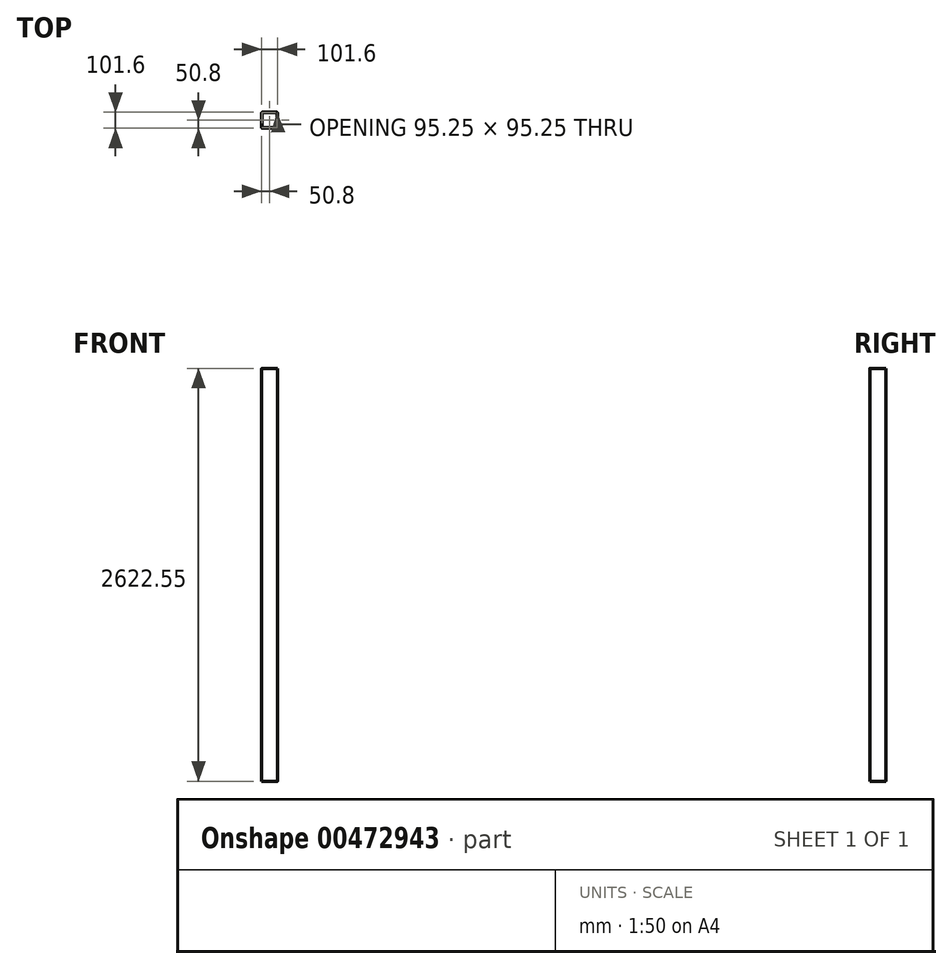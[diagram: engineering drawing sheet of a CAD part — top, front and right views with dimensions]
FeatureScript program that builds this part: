
annotation { "Feature Type Name" : "Feature", "Feature Type Description" : "" }
export const myFeature = defineFeature(function(context is Context, id is Id, definition is map)
    precondition{}
    {
        {
            var Q0;
            Q0=qCreatedBy(makeId("Top.planeOp"),FACE);
            var sketch = newSketch(context, id + "F0", { "sketchPlane" : qUnion([Q0])});
            skLineSegment(sketch, "E0.bottom", {"start": v(-50.8, -50.8) * mm, "end": v(50.8, -50.8) * mm});
            skLineSegment(sketch, "E0.top", {"start": v(-50.8, 50.8) * mm, "end": v(50.8, 50.8) * mm});
            skLineSegment(sketch, "E0.left", {"start": v(-50.8, -50.8) * mm, "end": v(-50.8, 50.8) * mm});
            skLineSegment(sketch, "E0.right", {"start": v(50.8, -50.8) * mm, "end": v(50.8, 50.8) * mm});
            skPoint(sketch, "E0.middle", {"position": v(0, 0) * mm});
            skLineSegment(sketch, "E1.bottom", {"start": v(-47.63, -47.63) * mm, "end": v(47.63, -47.63) * mm});
            skLineSegment(sketch, "E1.top", {"start": v(-47.63, 47.63) * mm, "end": v(47.63, 47.63) * mm});
            skLineSegment(sketch, "E1.left", {"start": v(-47.63, -47.63) * mm, "end": v(-47.63, 47.63) * mm});
            skLineSegment(sketch, "E1.right", {"start": v(47.63, -47.63) * mm, "end": v(47.63, 47.63) * mm});
            skSolve(sketch);
        }
        {
            var Q0;
            Q0=makeQuery(id+"F0.imprint","IMPRINT",FACE,{"disambiguationData":[TD([[makeQuery(id+"F0.imprint","IMPRINT",EDGE,{"derivedFrom":sQuery(id+"F0.wireOp",EDGE,"E0.bottom")}),1.0]])]});
            extrude(context, id + "F1", {"entities" : qUnion([Q0]), "depth" : 2622.55 * mm});
        }
        {
            var Q0;
            Q0=makeQuery(id+"F1.opExtrude","SWEPT_EDGE",EDGE,{"disambiguationData":[OSD([sQuery(id+"F0.wireOp",EDGE,"E0.bottom"),sQuery(id+"F0.wireOp",EDGE,"E0.left")])]});
            var Q1;
            Q1=makeQuery(id+"F1.opExtrude","SWEPT_EDGE",EDGE,{"disambiguationData":[OSD([sQuery(id+"F0.wireOp",EDGE,"E0.bottom"),sQuery(id+"F0.wireOp",EDGE,"E0.right")])]});
            var Q2;
            Q2=makeQuery(id+"F1.opExtrude","SWEPT_EDGE",EDGE,{"disambiguationData":[OSD([sQuery(id+"F0.wireOp",EDGE,"E0.top"),sQuery(id+"F0.wireOp",EDGE,"E0.right")])]});
            var Q3;
            Q3=makeQuery(id+"F1.opExtrude","SWEPT_EDGE",EDGE,{"disambiguationData":[OSD([sQuery(id+"F0.wireOp",EDGE,"E0.top"),sQuery(id+"F0.wireOp",EDGE,"E0.left")])]});
            var Q4;
            Q4=makeQuery(id+"F1.opExtrude","SWEPT_EDGE",EDGE,{"disambiguationData":[OSD([sQuery(id+"F0.wireOp",EDGE,"E1.bottom"),sQuery(id+"F0.wireOp",EDGE,"E1.right")])]});
            var Q5;
            Q5=makeQuery(id+"F1.opExtrude","SWEPT_EDGE",EDGE,{"disambiguationData":[OSD([sQuery(id+"F0.wireOp",EDGE,"E1.top"),sQuery(id+"F0.wireOp",EDGE,"E1.right")])]});
            var Q6;
            Q6=makeQuery(id+"F1.opExtrude","SWEPT_EDGE",EDGE,{"disambiguationData":[OSD([sQuery(id+"F0.wireOp",EDGE,"E1.top"),sQuery(id+"F0.wireOp",EDGE,"E1.left")])]});
            var Q7;
            Q7=makeQuery(id+"F1.opExtrude","SWEPT_EDGE",EDGE,{"disambiguationData":[OSD([sQuery(id+"F0.wireOp",EDGE,"E1.bottom"),sQuery(id+"F0.wireOp",EDGE,"E1.left")])]});
            fillet(context, id + "F2", {"entities" : qUnion([Q0, Q1, Q2, Q3, Q4, Q5, Q6, Q7]), "radius" : 5.08 * mm, "tangentPropagation" : true, "allowEdgeOverflow" : false});
        }
    });
